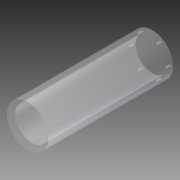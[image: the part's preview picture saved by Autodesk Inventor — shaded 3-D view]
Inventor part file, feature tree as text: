
AUTODESK INVENTOR PART (.ipt)
format: ipt  version: 2015 (Build 190159000, 159)  size: 105,472 bytes
history: native  units: mm
features: sketch x3, extrude x2, hole x1
ambient origin geometry x8: Origin, YZ Plane, XZ Plane, XY Plane, X Axis, Y Axis, Z Axis, Center Point
bodies: Solid1 (feature_tree)
feature tree (6):
  extrude  "Extrusion1"  Depth=56.0mm
  extrude  "Extrusion2"  Depth=7.0mm TaperAngle=0.0deg
  hole  "Hole1"  [1 undecoded]
  sketch  "Sketch1"  dims[d0=70.0mm d1=56.0mm]
  sketch  "Sketch2"  dims[d2=210.0mm d3=0.0mm d4=7.0mm d5=0.0mm]
  sketch  "Sketch3"  dims[d6=4.0mm d7=4.0mm d8=4.0mm d9=4.0mm d10=4.0mm d11=4.0mm d12=3.0mm d13=6.0mm d14=4.0mm d15=2.0mm d16=90.0deg d17=8.0mm d18=20.594885mm]
note: 1 required parameter value undecoded (feature->parameter linkage not recoverable at this tier; creation-order binding heuristic only, values carry confidence <= 0.55)
